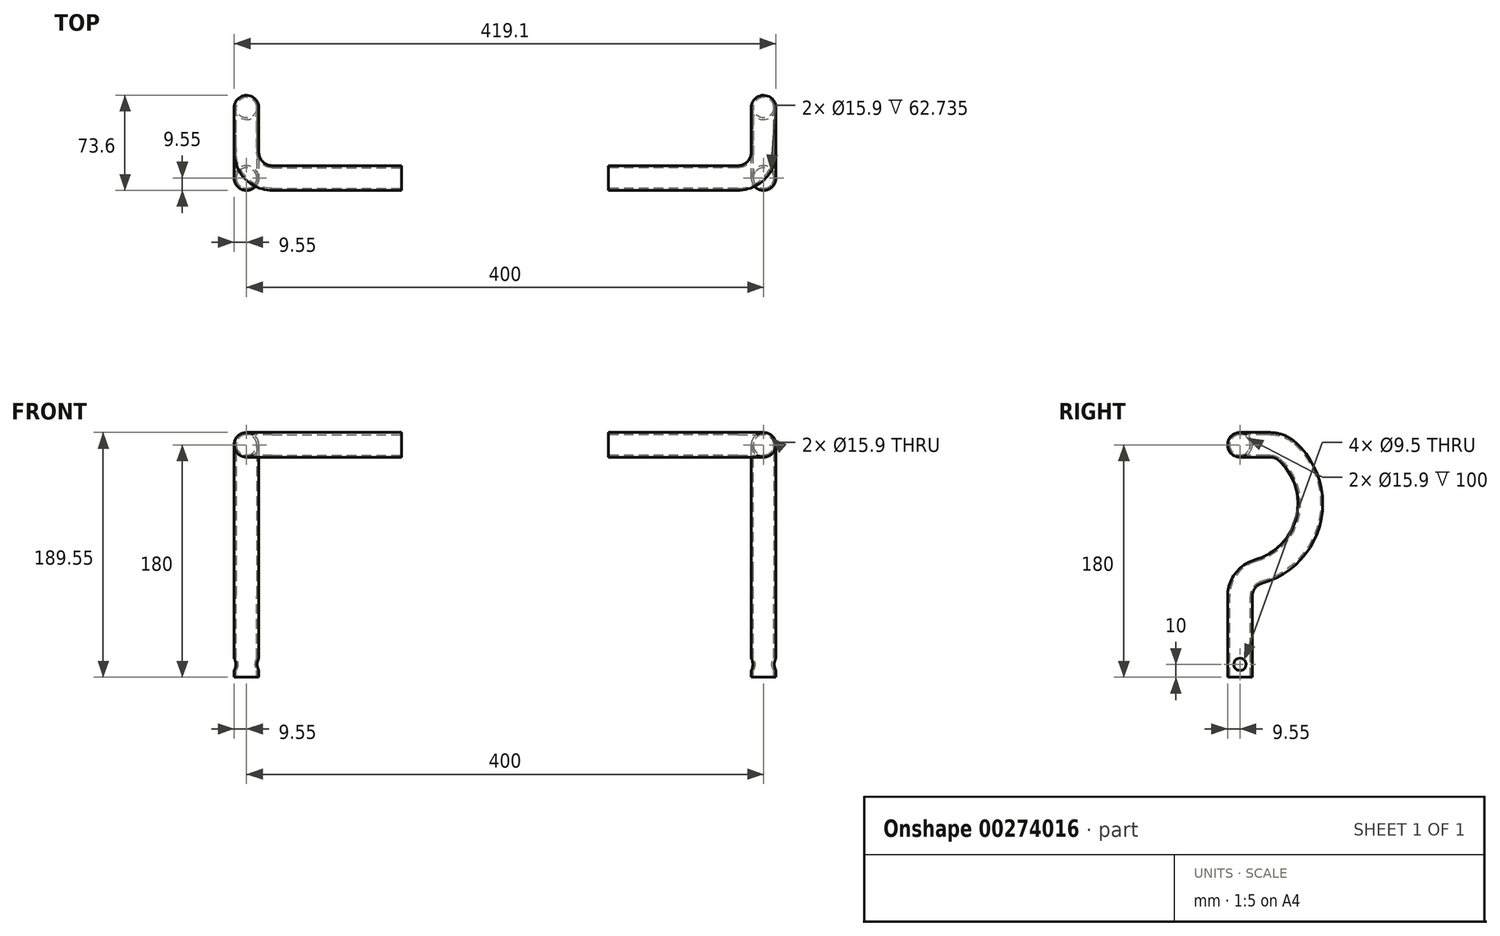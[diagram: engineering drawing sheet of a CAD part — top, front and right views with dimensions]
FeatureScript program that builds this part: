
annotation { "Feature Type Name" : "Feature", "Feature Type Description" : "" }
export const myFeature = defineFeature(function(context is Context, id is Id, definition is map)
    precondition{}
    {
        {
            var Q0;
            Q0=qCreatedBy(makeId("Right.planeOp"),FACE);
            var sketch = newSketch(context, id + "F0", { "sketchPlane" : qUnion([Q0])});
            skLineSegment(sketch, "E0", {"start": v(0, -117.27) * mm, "end": v(0, -180) * mm});
            skLineSegment(sketch, "E1", {"start": v(0, 0) * mm, "end": v(23.24, 0) * mm});
            skArc(sketch, "E2", {"start": v(14.63, -98) * mm, "mid": v(53.02, -58.12) * mm, "end": v(36.7, -5.22) * mm});
            skPoint(sketch, "E3.visualSharp", {"position": v(30, 0) * mm});
            skArc(sketch, "E3.filletArc", {"start": v(36.7, -5.22) * mm, "mid": v(30.46, -1.35) * mm, "end": v(23.24, 0) * mm});
            skPoint(sketch, "E4.visualSharp", {"position": v(0, -100) * mm});
            skArc(sketch, "E4.filletArc", {"start": v(14.63, -98) * mm, "mid": v(4.07, -105.17) * mm, "end": v(0, -117.27) * mm});
            skSolve(sketch);
        }
        {
            var Q0;
            Q0=qCreatedBy(makeId("Top.planeOp"),FACE);
            var sketch = newSketch(context, id + "F1", { "sketchPlane" : qUnion([Q0])});
            skLineSegment(sketch, "E5.0", {"start": v(0, 20) * mm, "end": v(0, 23.24) * mm});
            skLineSegment(sketch, "E6", {"start": v(-20, 0) * mm, "end": v(-120, 0) * mm});
            skPoint(sketch, "E7.visualSharp", {"position": v(0, 0) * mm});
            skArc(sketch, "E7.filletArc", {"start": v(-20, 0) * mm, "mid": v(-5.86, 5.86) * mm, "end": v(0, 20) * mm});
            skSolve(sketch);
        }
        {
            var Q0;
            Q0=sQuery(id+"F0.wireOp",VERTEX,"E0.end");
            var Q1;
            Q1=sQuery(id+"F0.wireOp",EDGE,"E0");
            cPlane(context, id + "F2", {"entities" : qUnion([Q0, Q1]), "cplaneType" : CPlaneType.LINE_POINT, "offset" : 150 * mm, "width" : 150 * mm, "height" : 150 * mm});
        }
        {
            var Q0;
            Q0=qCreatedBy(id+"F2.planeOp",FACE);
            var sketch = newSketch(context, id + "F3", { "sketchPlane" : qUnion([Q0])});
            skPoint(sketch, "E8.0", {"position": v(0, 0) * mm});
            skCircle(sketch, "E9", {"center": v(0, 0) * mm, "radius": 9.55 * mm});
            skCircle(sketch, "E10", {"center": v(0, 0) * mm, "radius": 7.95 * mm});
            skSolve(sketch);
        }
        {
            var Q0;
            Q0=makeQuery(id+"F3.imprint","IMPRINT",FACE,{"disambiguationData":[TD([[makeQuery(id+"F3.imprint","IMPRINT",EDGE,{"derivedFrom":sQuery(id+"F3.wireOp",EDGE,"E9")}),1.0]])]});
            var Q1;
            Q1=sQuery(id+"F0.wireOp",EDGE,"E0");
            var Q2;
            Q2=sQuery(id+"F0.wireOp",EDGE,"E4.filletArc");
            var Q3;
            Q3=sQuery(id+"F0.wireOp",EDGE,"E2");
            var Q4;
            Q4=sQuery(id+"F0.wireOp",EDGE,"E3.filletArc");
            var Q5;
            Q5=sQuery(id+"F1.wireOp",EDGE,"E5.0");
            var Q6;
            Q6=sQuery(id+"F1.wireOp",EDGE,"E7.filletArc");
            var Q7;
            Q7=sQuery(id+"F1.wireOp",EDGE,"E6");
            sweep(context, id + "F4", {"profiles" : qUnion([Q0]), "path" : qUnion([Q1, Q2, Q3, Q4, Q5, Q6, Q7])});
        }
        {
            var Q0;
            Q0=qCreatedBy(makeId("Right.planeOp"),FACE);
            var sketch = newSketch(context, id + "F5", { "sketchPlane" : qUnion([Q0])});
            skPoint(sketch, "E11.0", {"position": v(0, -180) * mm});
            skCircle(sketch, "E12", {"center": v(0, -170) * mm, "radius": 4.75 * mm});
            skSolve(sketch);
        }
        {
            var Q0;
            Q0=qSketchRegion(id+"F5",true);
            extrude(context, id + "F6", {"entities" : qUnion([Q0]), "operationType" : NewBodyOperationType.REMOVE, "endBound" : BoundingType.THROUGH_ALL, "oppositeDirection" : true, "depth" : 25 * mm, "hasSecondDirection" : true, "secondDirectionBound" : SecondDirectionBoundingType.THROUGH_ALL, "secondDirectionOppositeDirection" : false, "secondDirectionDepth" : 25 * mm});
        }
        {
            var Q0;
            Q0=qCreatedBy(makeId("Right.planeOp"),FACE);
            cPlane(context, id + "F7", {"entities" : qUnion([Q0]), "cplaneType" : CPlaneType.OFFSET, "offset" : 200 * mm, "oppositeDirection" : true, "width" : 150 * mm, "height" : 150 * mm});
        }
        {
            var Q0;
            Q0=makeQuery(id+"F4.opSweep","SWEPT_BODY",BODY,{"disambiguationData":[OSD([sQuery(id+"F1.wireOp",EDGE,"E6"),sQuery(id+"F3.wireOp",EDGE,"E9"),sQuery(id+"F3.wireOp",EDGE,"E10")])]});
            var Q1;
            Q1=qCreatedBy(id+"F7.planeOp",FACE);
            mirror(context, id + "F8", {"entities" : qUnion([Q0]), "mirrorPlane" : qUnion([Q1])});
        }
    });
